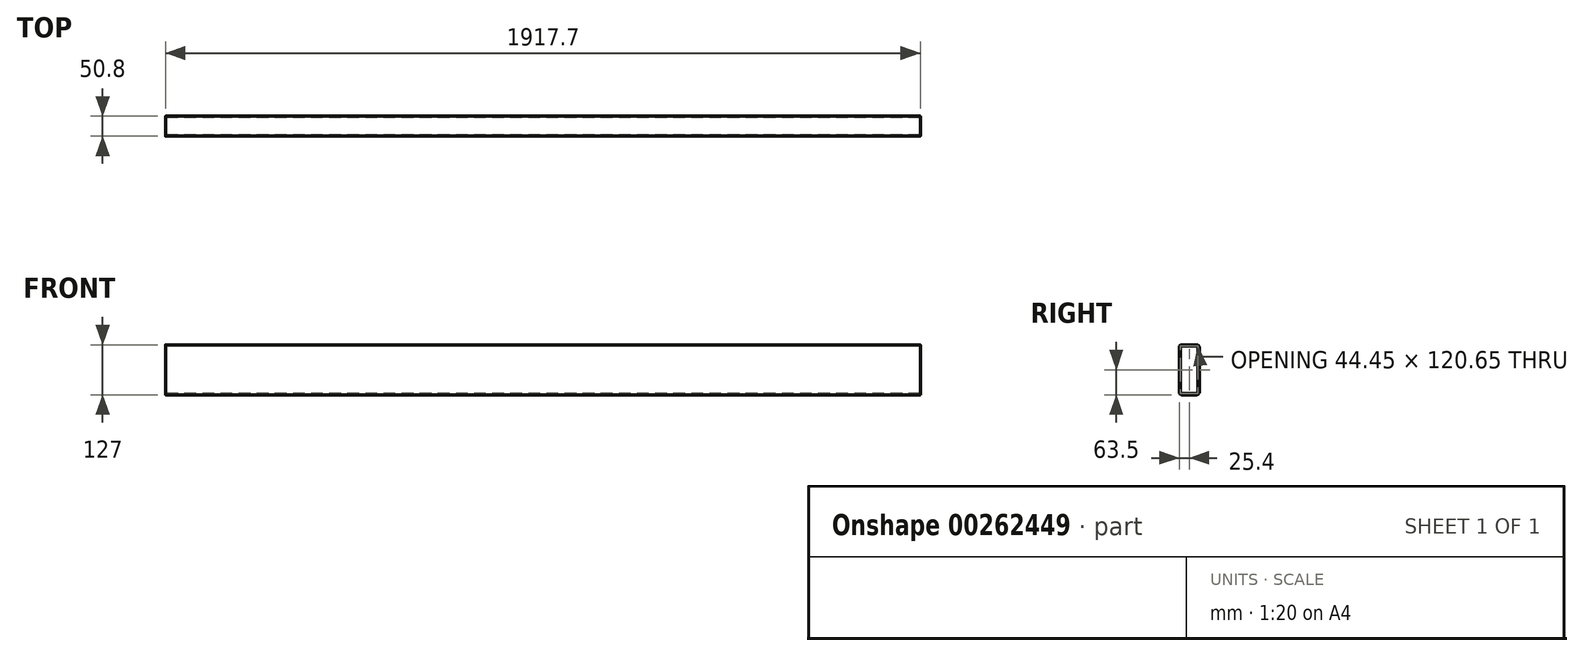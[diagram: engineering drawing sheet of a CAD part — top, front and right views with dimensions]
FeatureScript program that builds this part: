
annotation { "Feature Type Name" : "Feature", "Feature Type Description" : "" }
export const myFeature = defineFeature(function(context is Context, id is Id, definition is map)
    precondition{}
    {
        {
            var Q0;
            Q0=qCreatedBy(makeId("Right.planeOp"),FACE);
            var sketch = newSketch(context, id + "F0", { "sketchPlane" : qUnion([Q0])});
            skLineSegment(sketch, "E0.bottom", {"start": v(-19.05, 63.5) * mm, "end": v(19.05, 63.5) * mm});
            skLineSegment(sketch, "E0.top", {"start": v(-19.05, -63.5) * mm, "end": v(19.05, -63.5) * mm});
            skLineSegment(sketch, "E0.left", {"start": v(-25.4, 57.15) * mm, "end": v(-25.4, -57.15) * mm});
            skLineSegment(sketch, "E0.right", {"start": v(25.4, 57.15) * mm, "end": v(25.4, -57.15) * mm});
            skPoint(sketch, "E0.middle", {"position": v(0, 0) * mm});
            skLineSegment(sketch, "E1.bottom", {"start": v(15.88, 60.33) * mm, "end": v(-15.88, 60.33) * mm});
            skLineSegment(sketch, "E1.top", {"start": v(15.88, -60.33) * mm, "end": v(-15.88, -60.33) * mm});
            skLineSegment(sketch, "E1.left", {"start": v(22.23, 53.98) * mm, "end": v(22.23, -53.98) * mm});
            skLineSegment(sketch, "E1.right", {"start": v(-22.23, 53.98) * mm, "end": v(-22.23, -53.98) * mm});
            skPoint(sketch, "E2.visualSharp", {"position": v(-25.4, 63.5) * mm});
            skArc(sketch, "E2.filletArc", {"start": v(-19.05, 63.5) * mm, "mid": v(-23.54, 61.64) * mm, "end": v(-25.4, 57.15) * mm});
            skPoint(sketch, "E3.visualSharp", {"position": v(-22.23, 60.33) * mm});
            skArc(sketch, "E3.filletArc", {"start": v(-15.88, 60.33) * mm, "mid": v(-20.37, 58.47) * mm, "end": v(-22.23, 53.98) * mm});
            skPoint(sketch, "E4.visualSharp", {"position": v(25.4, 63.5) * mm});
            skArc(sketch, "E4.filletArc", {"start": v(25.4, 57.15) * mm, "mid": v(23.54, 61.64) * mm, "end": v(19.05, 63.5) * mm});
            skPoint(sketch, "E5.visualSharp", {"position": v(22.23, 60.33) * mm});
            skArc(sketch, "E5.filletArc", {"start": v(22.23, 53.98) * mm, "mid": v(20.37, 58.47) * mm, "end": v(15.88, 60.33) * mm});
            skPoint(sketch, "E6.visualSharp", {"position": v(-25.4, -63.5) * mm});
            skArc(sketch, "E6.filletArc", {"start": v(-25.4, -57.15) * mm, "mid": v(-23.54, -61.64) * mm, "end": v(-19.05, -63.5) * mm});
            skPoint(sketch, "E7.visualSharp", {"position": v(-22.23, -60.33) * mm});
            skArc(sketch, "E7.filletArc", {"start": v(-22.23, -53.98) * mm, "mid": v(-20.37, -58.47) * mm, "end": v(-15.88, -60.33) * mm});
            skPoint(sketch, "E8.visualSharp", {"position": v(22.23, -60.33) * mm});
            skArc(sketch, "E8.filletArc", {"start": v(15.88, -60.33) * mm, "mid": v(20.37, -58.47) * mm, "end": v(22.23, -53.98) * mm});
            skPoint(sketch, "E9.visualSharp", {"position": v(25.4, -63.5) * mm});
            skArc(sketch, "E9.filletArc", {"start": v(19.05, -63.5) * mm, "mid": v(23.54, -61.64) * mm, "end": v(25.4, -57.15) * mm});
            skSolve(sketch);
        }
        {
            var Q0;
            Q0 = qSketchRegion(id + "F0", true);
            extrude(context, id + "F1", {"entities" : qUnion([Q0]), "depth" : 1917.7 * mm});
        }
    });
